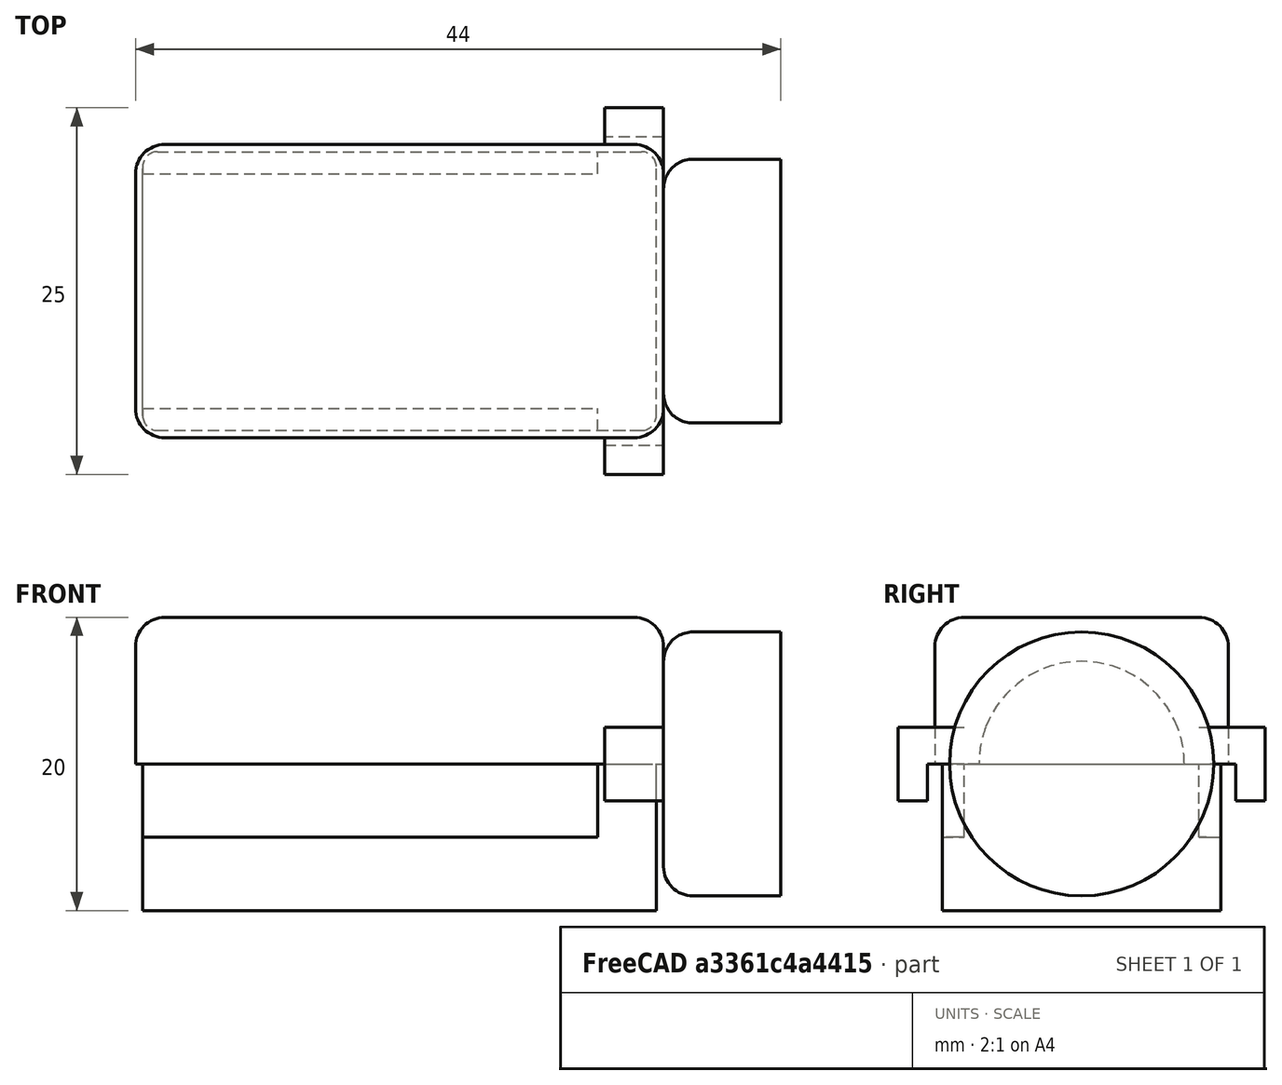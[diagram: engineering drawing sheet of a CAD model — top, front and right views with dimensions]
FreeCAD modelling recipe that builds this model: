
FCSTD DOCUMENT  (FreeCAD 0.21R33771 (Git))
Label: Ножка для вентилятора
License: All rights reserved
LicenseURL: http://en.wikipedia.org/wiki/All_rights_reserved
objects: Part::Box×6, Part::Fillet×3, Part::MultiFuse×2, Part::Cut×2, Part::Cylinder×1
note: 14 computed .brp shape members not serialized (recipe doc carries the construction recipe); baked Part::Feature solids carry a one-line shape summary decoded from their .brp

FEATURE [Part::Box] Box  label="Куб"
  AttacherType = Attacher::AttachEngine3D
  Height = 10
  Length = 35
  Width = 19
FEATURE [Part::Box] Box001  label="Куб001"
  AttacherType = Attacher::AttachEngine3D
  Height = 5
  Length = 32
  Placement = pos=(-1,-0.5,5) rot=(0,0,1;0rad)
  Width = 2
FEATURE [Part::Box] Box002  label="Куб002"
  AttacherType = Attacher::AttachEngine3D
  Height = 5
  Length = 32
  Placement = pos=(-1,17.5,5) rot=(0,0,1;0rad)
  Width = 2
FEATURE [Part::Box] Box003  label="Куб003"
  AttacherType = Attacher::AttachEngine3D
  Height = 10
  Length = 36
  Placement = pos=(-0.5,-0.5,10) rot=(0,0,1;0rad)
  Width = 20
FEATURE [Part::Box] Box004  label="Куб004"
  AttacherType = Attacher::AttachEngine3D
  Height = 5
  Length = 4
  Placement = pos=(31.5,-3,7.5) rot=(0,0,1;0rad)
  Width = 25
FEATURE [Part::MultiFuse] Fusion
  Refine = true
  Shapes = -> [Box001,Box002]
FEATURE [Part::Cut] Cut
  Base = -> Box
  Refine = true
  Tool = -> Fusion
FEATURE [Part::Cylinder] Cylinder  label="Цилиндр"
  Angle = 360
  AttacherType = Attacher::AttachEngine3D
  FirstAngle = 0
  Height = 8
  Placement = pos=(35.5,9.5,10) rot=(0,1,0;1.5708rad)
  Radius = 9
  SecondAngle = 0
FEATURE [Part::Fillet] Fillet
  Base = -> Cylinder
  Edges = 1 edges r=2: [Edge2]
FEATURE [Part::Fillet] Fillet001
  Base = -> Cut
  Edges = 4 edges r=1: [Edge1,Edge7,Edge9,Edge27]
FEATURE [Part::Fillet] Fillet002
  Base = -> Box003
  Edges = 8 edges r=2: [Edge1,Edge2,Edge3,Edge5,Edge6,Edge7,Edge10,Edge12]
FEATURE [Part::Box] Box005  label="Куб005"
  AttacherType = Attacher::AttachEngine3D
  Height = 3
  Length = 6
  Placement = pos=(30.5,-1,7) rot=(0,0,1;0rad)
  Width = 21
FEATURE [Part::Cut] Cut001
  Base = -> Box004
  Refine = true
  Tool = -> Box005
FEATURE [Part::MultiFuse] Fusion001
  Refine = true
  Shapes = -> [Fillet,Fillet001,Fillet002,Cut001]
